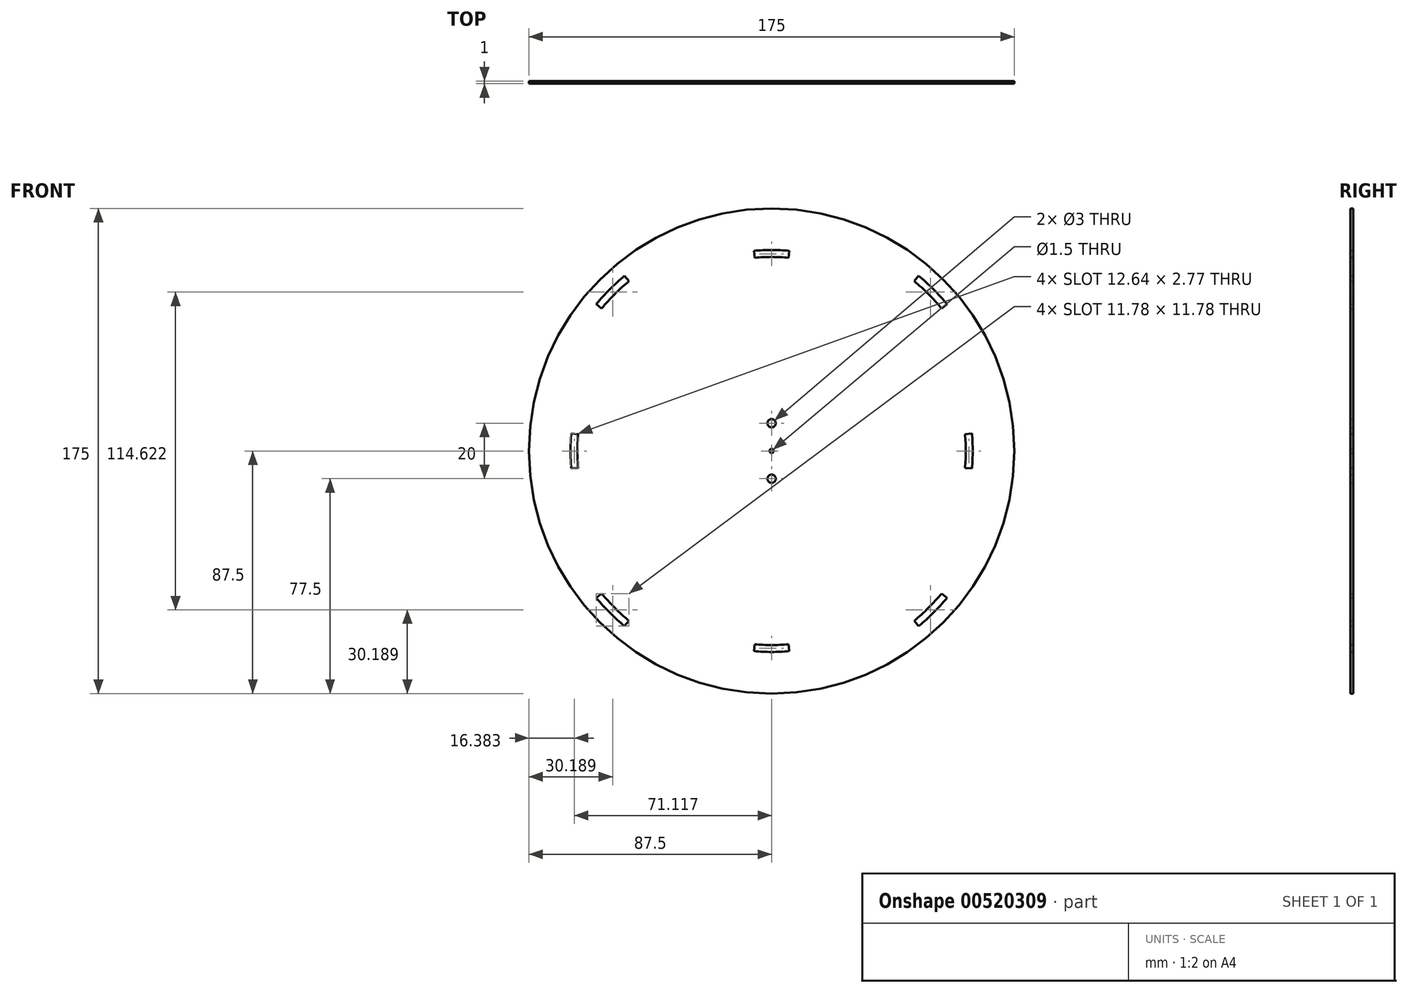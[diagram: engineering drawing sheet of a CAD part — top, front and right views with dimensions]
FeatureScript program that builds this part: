
annotation { "Feature Type Name" : "Feature", "Feature Type Description" : "" }
export const myFeature = defineFeature(function(context is Context, id is Id, definition is map)
    precondition{}
    {
        {
            var Q0;
            Q0=qCreatedBy(makeId("Front.planeOp"),FACE);
            var sketch = newSketch(context, id + "F0", { "sketchPlane" : qUnion([Q0])});
            skCircle(sketch, "E0", {"center": v(0, 0) * mm, "radius": 87.5 * mm});
            skCircle(sketch, "E1", {"center": v(0, 10) * mm, "radius": 1.5 * mm});
            skCircle(sketch, "E2", {"center": v(0, -10) * mm, "radius": 1.5 * mm});
            skLineSegment(sketch, "E3", {"start": v(51.42, -61.28) * mm, "end": v(53.03, -63.2) * mm});
            skLineSegment(sketch, "E4", {"start": v(63.2, -53.03) * mm, "end": v(61.28, -51.42) * mm});
            skArc(sketch, "E5", {"start": v(51.42, -61.28) * mm, "mid": v(56.57, -56.57) * mm, "end": v(61.28, -51.42) * mm});
            skArc(sketch, "E6", {"start": v(53.03, -63.2) * mm, "mid": v(58.34, -58.34) * mm, "end": v(63.2, -53.03) * mm});
            skLineSegment(sketch, "E7", {"start": v(-63.2, -53.03) * mm, "end": v(-61.28, -51.42) * mm});
            skLineSegment(sketch, "E8", {"start": v(-53.03, -63.2) * mm, "end": v(-51.42, -61.28) * mm});
            skArc(sketch, "E9", {"start": v(-61.28, -51.42) * mm, "mid": v(-56.57, -56.57) * mm, "end": v(-51.42, -61.28) * mm});
            skArc(sketch, "E10", {"start": v(-63.2, -53.03) * mm, "mid": v(-58.34, -58.34) * mm, "end": v(-53.03, -63.2) * mm});
            skLineSegment(sketch, "E11", {"start": v(-53.03, 63.2) * mm, "end": v(-51.42, 61.28) * mm});
            skLineSegment(sketch, "E12", {"start": v(-63.2, 53.03) * mm, "end": v(-61.28, 51.42) * mm});
            skArc(sketch, "E13", {"start": v(-61.28, 51.42) * mm, "mid": v(-56.57, 56.57) * mm, "end": v(-51.42, 61.28) * mm});
            skArc(sketch, "E14", {"start": v(-63.2, 53.03) * mm, "mid": v(-58.34, 58.34) * mm, "end": v(-53.03, 63.2) * mm});
            skLineSegment(sketch, "E15", {"start": v(63.2, 53.03) * mm, "end": v(61.28, 51.42) * mm});
            skLineSegment(sketch, "E16", {"start": v(53.03, 63.2) * mm, "end": v(51.42, 61.28) * mm});
            skArc(sketch, "E17", {"start": v(51.42, 61.28) * mm, "mid": v(56.57, 56.57) * mm, "end": v(61.28, 51.42) * mm});
            skArc(sketch, "E18", {"start": v(63.2, 53.03) * mm, "mid": v(58.34, 58.34) * mm, "end": v(53.03, 63.2) * mm});
            skLineSegment(sketch, "E19", {"start": v(-6.1, -69.73) * mm, "end": v(-6.32, -72.22) * mm});
            skLineSegment(sketch, "E20", {"start": v(6.32, -72.22) * mm, "end": v(6.1, -69.73) * mm});
            skArc(sketch, "E21", {"start": v(-6.1, -69.73) * mm, "mid": v(0, -70) * mm, "end": v(6.1, -69.73) * mm});
            skArc(sketch, "E22", {"start": v(-6.32, -72.22) * mm, "mid": v(0, -72.5) * mm, "end": v(6.32, -72.22) * mm});
            skLineSegment(sketch, "E23", {"start": v(-72.22, 6.32) * mm, "end": v(-69.73, 6.1) * mm});
            skLineSegment(sketch, "E24", {"start": v(-72.22, -6.32) * mm, "end": v(-69.73, -6.1) * mm});
            skArc(sketch, "E25", {"start": v(-69.73, 6.1) * mm, "mid": v(-70, 0) * mm, "end": v(-69.73, -6.1) * mm});
            skArc(sketch, "E26", {"start": v(-72.22, 6.32) * mm, "mid": v(-72.5, 0) * mm, "end": v(-72.22, -6.32) * mm});
            skLineSegment(sketch, "E27", {"start": v(6.32, 72.22) * mm, "end": v(6.1, 69.73) * mm});
            skLineSegment(sketch, "E28", {"start": v(-6.32, 72.22) * mm, "end": v(-6.1, 69.73) * mm});
            skArc(sketch, "E29", {"start": v(-6.1, 69.73) * mm, "mid": v(0, 70) * mm, "end": v(6.1, 69.73) * mm});
            skArc(sketch, "E30", {"start": v(-6.32, 72.22) * mm, "mid": v(0, 72.5) * mm, "end": v(6.32, 72.22) * mm});
            skLineSegment(sketch, "E31", {"start": v(72.22, -6.32) * mm, "end": v(69.73, -6.1) * mm});
            skLineSegment(sketch, "E32", {"start": v(72.22, 6.32) * mm, "end": v(69.73, 6.1) * mm});
            skArc(sketch, "E33", {"start": v(69.73, 6.1) * mm, "mid": v(70, 0) * mm, "end": v(69.73, -6.1) * mm});
            skArc(sketch, "E34", {"start": v(72.22, -6.32) * mm, "mid": v(72.5, 0) * mm, "end": v(72.22, 6.32) * mm});
            skCircle(sketch, "E35", {"center": v(0, 0) * mm, "radius": 0.75 * mm});
            skSolve(sketch);
        }
        {
            var Q0;
            Q0 = qSketchRegion(id + "F0", true);
            extrude(context, id + "F1", {"entities" : qUnion([Q0]), "depth" : 1 * mm, "offsetDistance" : 25 * mm});
        }
    });
